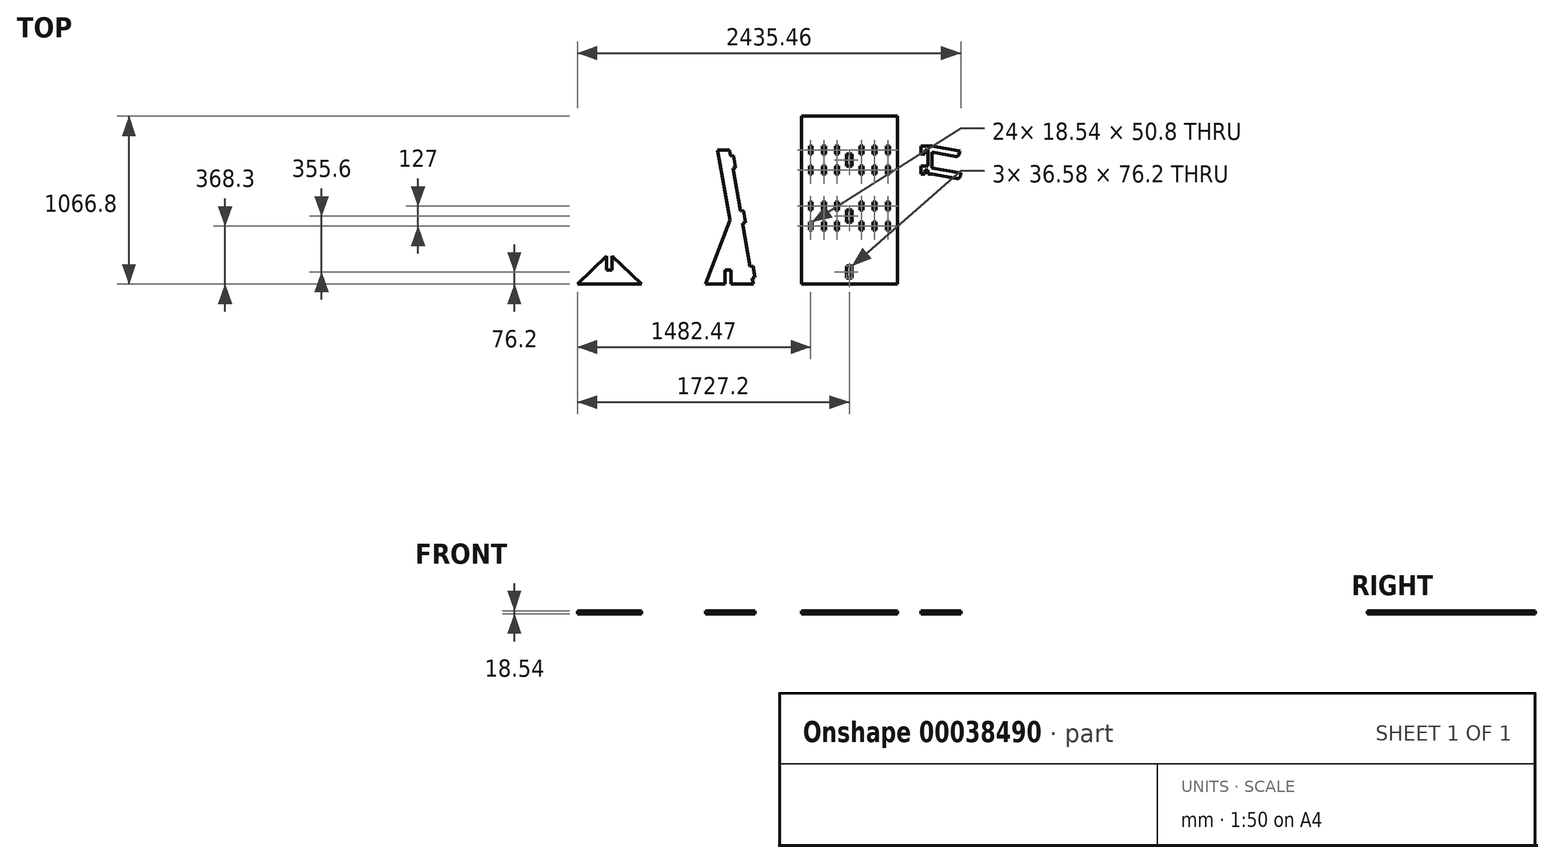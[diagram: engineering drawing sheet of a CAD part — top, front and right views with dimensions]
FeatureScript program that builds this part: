
annotation { "Feature Type Name" : "Feature", "Feature Type Description" : "" }
export const myFeature = defineFeature(function(context is Context, id is Id, definition is map)
    precondition{}
    {
        {
            var Q0;
            Q0=qCreatedBy(makeId("Top.planeOp"),FACE);
            var sketch = newSketch(context, id + "F0", { "sketchPlane" : qUnion([Q0])});
            skLineSegment(sketch, "E0", {"start": v(0, 0) * mm, "end": v(304.8, 0) * mm});
            skLineSegment(sketch, "E1", {"start": v(304.8, 0) * mm, "end": v(154.84, 850.48) * mm});
            skLineSegment(sketch, "E2", {"start": v(154.84, 850.48) * mm, "end": v(78.64, 850.48) * mm});
            skLineSegment(sketch, "E3", {"start": v(78.64, 850.48) * mm, "end": v(0, 0) * mm});
            skLineSegment(sketch, "E4", {"start": v(78.64, 850.48) * mm, "end": v(156.94, 406.4) * mm});
            skLineSegment(sketch, "E5", {"start": v(156.94, 406.4) * mm, "end": v(0, 0) * mm});
            skLineSegment(sketch, "E6", {"start": v(161.45, 812.96) * mm, "end": v(179.71, 816.18) * mm});
            skLineSegment(sketch, "E7", {"start": v(179.71, 816.18) * mm, "end": v(192.95, 741.14) * mm});
            skLineSegment(sketch, "E8", {"start": v(192.95, 741.14) * mm, "end": v(174.69, 737.92) * mm});
            skLineSegment(sketch, "E9", {"start": v(229.82, 425.24) * mm, "end": v(248.08, 428.46) * mm, "construction": true});
            skLineSegment(sketch, "E10.0", {"start": v(223.2, 462.76) * mm, "end": v(241.46, 465.98) * mm});
            skLineSegment(sketch, "E11.0", {"start": v(236.43, 387.72) * mm, "end": v(254.7, 390.94) * mm});
            skLineSegment(sketch, "E12", {"start": v(241.46, 465.98) * mm, "end": v(254.7, 390.94) * mm});
            skLineSegment(sketch, "E13.MirrorCS", {"start": v(298.18, 37.52) * mm, "end": v(316.44, 40.74) * mm});
            skLineSegment(sketch, "E14.MirrorCS", {"start": v(316.44, 40.74) * mm, "end": v(303.21, 115.78) * mm});
            skLineSegment(sketch, "E15.MirrorCS", {"start": v(303.21, 115.78) * mm, "end": v(284.95, 112.56) * mm});
            skLineSegment(sketch, "E16.bottom", {"start": v(127, 0) * mm, "end": v(164.08, 0) * mm});
            skLineSegment(sketch, "E16.top", {"start": v(127, 88.9) * mm, "end": v(164.08, 88.9) * mm});
            skLineSegment(sketch, "E16.left", {"start": v(127, 0) * mm, "end": v(127, 88.9) * mm});
            skLineSegment(sketch, "E16.right", {"start": v(164.08, 0) * mm, "end": v(164.08, 88.9) * mm});
            skLineSegment(sketch, "E17.bottom", {"start": v(609.6, 1066.8) * mm, "end": v(1219.2, 1066.8) * mm});
            skLineSegment(sketch, "E17.top", {"start": v(609.6, 0) * mm, "end": v(1219.2, 0) * mm});
            skLineSegment(sketch, "E17.left", {"start": v(609.6, 1066.8) * mm, "end": v(609.6, 0) * mm});
            skLineSegment(sketch, "E17.right", {"start": v(1219.2, 1066.8) * mm, "end": v(1219.2, 0) * mm});
            skLineSegment(sketch, "E18.bottom", {"start": v(896.11, 825.5) * mm, "end": v(932.69, 825.5) * mm});
            skLineSegment(sketch, "E18.top", {"start": v(896.11, 749.3) * mm, "end": v(932.69, 749.3) * mm});
            skLineSegment(sketch, "E18.left", {"start": v(896.11, 825.5) * mm, "end": v(896.11, 749.3) * mm});
            skLineSegment(sketch, "E18.right", {"start": v(932.69, 825.5) * mm, "end": v(932.69, 749.3) * mm});
            skLineSegment(sketch, "E19.bottom", {"start": v(896.11, 469.9) * mm, "end": v(932.69, 469.9) * mm});
            skLineSegment(sketch, "E19.top", {"start": v(896.11, 393.7) * mm, "end": v(932.69, 393.7) * mm});
            skLineSegment(sketch, "E19.left", {"start": v(896.11, 469.9) * mm, "end": v(896.11, 393.7) * mm});
            skLineSegment(sketch, "E19.right", {"start": v(932.69, 469.9) * mm, "end": v(932.69, 393.7) * mm});
            skLineSegment(sketch, "E20.bottom", {"start": v(896.11, 114.3) * mm, "end": v(932.69, 114.3) * mm});
            skLineSegment(sketch, "E20.top", {"start": v(896.11, 38.1) * mm, "end": v(932.69, 38.1) * mm});
            skLineSegment(sketch, "E20.left", {"start": v(896.11, 114.3) * mm, "end": v(896.11, 38.1) * mm});
            skLineSegment(sketch, "E20.right", {"start": v(932.69, 114.3) * mm, "end": v(932.69, 38.1) * mm});
            skLineSegment(sketch, "E21", {"start": v(914.4, 1066.8) * mm, "end": v(914.4, 825.5) * mm, "construction": true});
            skPoint(sketch, "E22", {"position": v(914.4, 825.5) * mm});
            skLineSegment(sketch, "E23.top", {"start": v(845.31, 469.9) * mm, "end": v(660.4, 469.9) * mm, "construction": true});
            skLineSegment(sketch, "E24", {"start": v(609.6, 431.8) * mm, "end": v(1219.2, 431.8) * mm, "construction": true});
            skPoint(sketch, "E24.startSnap0", {"position": v(896.11, 431.8) * mm});
            skLineSegment(sketch, "E25.bottom", {"start": v(660.4, 825.5) * mm, "end": v(845.31, 825.5) * mm, "construction": true});
            skLineSegment(sketch, "E25.top", {"start": v(660.4, 876.3) * mm, "end": v(845.31, 876.3) * mm, "construction": true});
            skLineSegment(sketch, "E25.left", {"start": v(660.4, 825.5) * mm, "end": v(660.4, 876.3) * mm});
            skLineSegment(sketch, "E25.right", {"start": v(845.31, 825.5) * mm, "end": v(845.31, 876.3) * mm});
            skLineSegment(sketch, "E26.bottom", {"start": v(660.4, 876.3) * mm, "end": v(678.94, 876.3) * mm});
            skLineSegment(sketch, "E26.top", {"start": v(660.4, 825.5) * mm, "end": v(678.94, 825.5) * mm});
            skLineSegment(sketch, "E26.left", {"start": v(660.4, 876.3) * mm, "end": v(660.4, 825.5) * mm});
            skLineSegment(sketch, "E26.right", {"start": v(678.94, 876.3) * mm, "end": v(678.94, 825.5) * mm});
            skLineSegment(sketch, "E27.bottom", {"start": v(762.13, 876.3) * mm, "end": v(743.58, 876.3) * mm});
            skLineSegment(sketch, "E27.top", {"start": v(762.13, 825.5) * mm, "end": v(743.58, 825.5) * mm});
            skLineSegment(sketch, "E27.left", {"start": v(762.13, 876.3) * mm, "end": v(762.13, 825.5) * mm});
            skLineSegment(sketch, "E27.right", {"start": v(743.58, 876.3) * mm, "end": v(743.58, 825.5) * mm});
            skPoint(sketch, "E27.middle", {"position": v(752.86, 850.9) * mm});
            skPoint(sketch, "E27.middle.positionSnap0", {"position": v(660.4, 850.9) * mm});
            skPoint(sketch, "E27.middle.positionSnap1", {"position": v(752.86, 825.5) * mm});
            skPoint(sketch, "E27.centerSnap0", {"position": v(660.4, 850.9) * mm});
            skPoint(sketch, "E27.centerSnap1", {"position": v(752.86, 825.5) * mm});
            skLineSegment(sketch, "E28.bottom", {"start": v(845.31, 876.3) * mm, "end": v(826.77, 876.3) * mm});
            skLineSegment(sketch, "E28.top", {"start": v(845.31, 825.5) * mm, "end": v(826.77, 825.5) * mm});
            skLineSegment(sketch, "E28.left", {"start": v(845.31, 876.3) * mm, "end": v(845.31, 825.5) * mm});
            skLineSegment(sketch, "E28.right", {"start": v(826.77, 876.3) * mm, "end": v(826.77, 825.5) * mm});
            skLineSegment(sketch, "E29.bottom", {"start": v(660.4, 749.3) * mm, "end": v(845.31, 749.3) * mm, "construction": true});
            skLineSegment(sketch, "E29.top", {"start": v(660.4, 698.5) * mm, "end": v(845.31, 698.5) * mm, "construction": true});
            skLineSegment(sketch, "E29.left", {"start": v(660.4, 749.3) * mm, "end": v(660.4, 698.5) * mm});
            skLineSegment(sketch, "E29.right", {"start": v(845.31, 749.3) * mm, "end": v(845.31, 698.5) * mm});
            skLineSegment(sketch, "E30.top", {"start": v(660.4, 520.7) * mm, "end": v(845.31, 520.7) * mm, "construction": true});
            skLineSegment(sketch, "E30.left", {"start": v(660.4, 469.9) * mm, "end": v(660.4, 520.7) * mm});
            skLineSegment(sketch, "E30.right", {"start": v(845.31, 469.9) * mm, "end": v(845.31, 520.7) * mm});
            skLineSegment(sketch, "E31.MirrorCS", {"start": v(660.4, 342.9) * mm, "end": v(845.31, 342.9) * mm, "construction": true});
            skLineSegment(sketch, "E32.MirrorCS", {"start": v(845.31, 393.7) * mm, "end": v(845.31, 342.9) * mm});
            skLineSegment(sketch, "E33.MirrorCS", {"start": v(845.31, 393.7) * mm, "end": v(660.4, 393.7) * mm, "construction": true});
            skLineSegment(sketch, "E34.MirrorCS", {"start": v(660.4, 393.7) * mm, "end": v(660.4, 342.9) * mm});
            skLineSegment(sketch, "E35.bottom", {"start": v(660.4, 749.3) * mm, "end": v(678.94, 749.3) * mm});
            skLineSegment(sketch, "E35.top", {"start": v(660.4, 698.5) * mm, "end": v(678.94, 698.5) * mm});
            skLineSegment(sketch, "E35.right", {"start": v(678.94, 749.3) * mm, "end": v(678.94, 698.5) * mm});
            skLineSegment(sketch, "E36.bottom", {"start": v(845.31, 749.3) * mm, "end": v(826.77, 749.3) * mm});
            skLineSegment(sketch, "E36.top", {"start": v(845.31, 698.5) * mm, "end": v(826.77, 698.5) * mm});
            skLineSegment(sketch, "E36.right", {"start": v(826.77, 749.3) * mm, "end": v(826.77, 698.5) * mm});
            skLineSegment(sketch, "E37.bottom", {"start": v(845.31, 520.7) * mm, "end": v(826.77, 520.7) * mm});
            skLineSegment(sketch, "E37.top", {"start": v(845.31, 469.9) * mm, "end": v(826.77, 469.9) * mm});
            skLineSegment(sketch, "E37.left", {"start": v(845.31, 520.7) * mm, "end": v(845.31, 469.9) * mm});
            skLineSegment(sketch, "E37.right", {"start": v(826.77, 520.7) * mm, "end": v(826.77, 469.9) * mm});
            skLineSegment(sketch, "E38.bottom", {"start": v(845.31, 393.7) * mm, "end": v(826.77, 393.7) * mm});
            skLineSegment(sketch, "E38.top", {"start": v(845.31, 342.9) * mm, "end": v(826.77, 342.9) * mm});
            skLineSegment(sketch, "E38.right", {"start": v(826.77, 393.7) * mm, "end": v(826.77, 342.9) * mm});
            skLineSegment(sketch, "E39.bottom", {"start": v(660.4, 393.7) * mm, "end": v(678.94, 393.7) * mm});
            skLineSegment(sketch, "E39.top", {"start": v(660.4, 342.9) * mm, "end": v(678.94, 342.9) * mm});
            skLineSegment(sketch, "E39.right", {"start": v(678.94, 393.7) * mm, "end": v(678.94, 342.9) * mm});
            skLineSegment(sketch, "E40.bottom", {"start": v(660.4, 469.9) * mm, "end": v(678.94, 469.9) * mm});
            skLineSegment(sketch, "E40.top", {"start": v(660.4, 520.7) * mm, "end": v(678.94, 520.7) * mm});
            skLineSegment(sketch, "E40.right", {"start": v(678.94, 469.9) * mm, "end": v(678.94, 520.7) * mm});
            skLineSegment(sketch, "E41.bottom", {"start": v(743.58, 749.3) * mm, "end": v(762.13, 749.3) * mm});
            skLineSegment(sketch, "E41.top", {"start": v(743.58, 698.5) * mm, "end": v(762.13, 698.5) * mm});
            skLineSegment(sketch, "E41.left", {"start": v(743.58, 749.3) * mm, "end": v(743.58, 698.5) * mm});
            skLineSegment(sketch, "E41.right", {"start": v(762.13, 749.3) * mm, "end": v(762.13, 698.5) * mm});
            skPoint(sketch, "E41.middle", {"position": v(752.86, 723.9) * mm});
            skPoint(sketch, "E41.middle.positionSnap0", {"position": v(678.94, 723.9) * mm});
            skPoint(sketch, "E41.middle.positionSnap1", {"position": v(752.86, 749.3) * mm});
            skPoint(sketch, "E41.centerSnap0", {"position": v(678.94, 723.9) * mm});
            skPoint(sketch, "E41.centerSnap1", {"position": v(752.86, 749.3) * mm});
            skLineSegment(sketch, "E42.bottom", {"start": v(743.58, 520.7) * mm, "end": v(762.13, 520.7) * mm});
            skLineSegment(sketch, "E42.top", {"start": v(743.58, 469.9) * mm, "end": v(762.13, 469.9) * mm});
            skLineSegment(sketch, "E42.left", {"start": v(743.58, 520.7) * mm, "end": v(743.58, 469.9) * mm});
            skLineSegment(sketch, "E42.right", {"start": v(762.13, 520.7) * mm, "end": v(762.13, 469.9) * mm});
            skPoint(sketch, "E42.middle", {"position": v(752.86, 495.3) * mm});
            skPoint(sketch, "E42.middle.positionSnap0", {"position": v(678.94, 495.3) * mm});
            skPoint(sketch, "E42.middle.positionSnap1", {"position": v(752.86, 520.7) * mm});
            skPoint(sketch, "E42.centerSnap0", {"position": v(678.94, 495.3) * mm});
            skPoint(sketch, "E42.centerSnap1", {"position": v(752.86, 520.7) * mm});
            skLineSegment(sketch, "E43.bottom", {"start": v(743.58, 393.7) * mm, "end": v(762.13, 393.7) * mm});
            skLineSegment(sketch, "E43.top", {"start": v(743.58, 342.9) * mm, "end": v(762.13, 342.9) * mm});
            skLineSegment(sketch, "E43.left", {"start": v(743.58, 393.7) * mm, "end": v(743.58, 342.9) * mm});
            skLineSegment(sketch, "E43.right", {"start": v(762.13, 393.7) * mm, "end": v(762.13, 342.9) * mm});
            skPoint(sketch, "E43.middle", {"position": v(752.86, 368.3) * mm});
            skPoint(sketch, "E43.middle.positionSnap0", {"position": v(678.94, 368.3) * mm});
            skPoint(sketch, "E43.middle.positionSnap1", {"position": v(752.86, 393.7) * mm});
            skPoint(sketch, "E43.centerSnap0", {"position": v(678.94, 368.3) * mm});
            skPoint(sketch, "E43.centerSnap1", {"position": v(752.86, 393.7) * mm});
            skLineSegment(sketch, "E44.MirrorCS", {"start": v(1168.4, 876.3) * mm, "end": v(1149.86, 876.3) * mm});
            skLineSegment(sketch, "E45.MirrorCS", {"start": v(1168.4, 825.5) * mm, "end": v(1168.4, 876.3) * mm});
            skLineSegment(sketch, "E46.MirrorCS", {"start": v(1149.86, 876.3) * mm, "end": v(1149.86, 825.5) * mm});
            skLineSegment(sketch, "E47.MirrorCS", {"start": v(1168.4, 825.5) * mm, "end": v(1149.86, 825.5) * mm});
            skLineSegment(sketch, "E48.MirrorCS", {"start": v(1066.67, 825.5) * mm, "end": v(1085.21, 825.5) * mm});
            skPoint(sketch, "E49.MirrorP", {"position": v(1075.94, 825.5) * mm});
            skLineSegment(sketch, "E50.MirrorCS", {"start": v(1085.22, 876.3) * mm, "end": v(1085.22, 825.5) * mm});
            skLineSegment(sketch, "E51.MirrorCS", {"start": v(1066.67, 876.3) * mm, "end": v(1066.67, 825.5) * mm});
            skPoint(sketch, "E52.MirrorP", {"position": v(1075.94, 850.9) * mm});
            skLineSegment(sketch, "E53.MirrorCS", {"start": v(1066.67, 876.3) * mm, "end": v(1085.21, 876.3) * mm});
            skLineSegment(sketch, "E54.MirrorCS", {"start": v(983.49, 876.3) * mm, "end": v(1002.03, 876.3) * mm});
            skLineSegment(sketch, "E55.MirrorCS", {"start": v(983.49, 876.3) * mm, "end": v(983.49, 825.5) * mm});
            skLineSegment(sketch, "E56.MirrorCS", {"start": v(983.49, 825.5) * mm, "end": v(1002.03, 825.5) * mm});
            skLineSegment(sketch, "E57.MirrorCS", {"start": v(1002.03, 876.3) * mm, "end": v(1002.03, 825.5) * mm});
            skLineSegment(sketch, "E58.MirrorCS", {"start": v(983.49, 749.3) * mm, "end": v(983.49, 698.5) * mm});
            skLineSegment(sketch, "E59.MirrorCS", {"start": v(1168.4, 749.3) * mm, "end": v(1168.4, 698.5) * mm});
            skLineSegment(sketch, "E60.MirrorCS", {"start": v(1168.4, 469.9) * mm, "end": v(1168.4, 520.7) * mm});
            skLineSegment(sketch, "E61.MirrorCS", {"start": v(983.49, 520.7) * mm, "end": v(983.49, 469.9) * mm});
            skLineSegment(sketch, "E62.MirrorCS", {"start": v(1168.4, 749.3) * mm, "end": v(1149.86, 749.3) * mm});
            skLineSegment(sketch, "E63.MirrorCS", {"start": v(1168.4, 698.5) * mm, "end": v(1149.86, 698.5) * mm});
            skLineSegment(sketch, "E64.MirrorCS", {"start": v(1085.21, 749.3) * mm, "end": v(1066.67, 749.3) * mm});
            skPoint(sketch, "E65.MirrorP", {"position": v(1075.94, 749.3) * mm});
            skLineSegment(sketch, "E66.MirrorCS", {"start": v(1066.67, 749.3) * mm, "end": v(1066.67, 698.5) * mm});
            skLineSegment(sketch, "E67.MirrorCS", {"start": v(1085.21, 698.5) * mm, "end": v(1066.67, 698.5) * mm});
            skPoint(sketch, "E68.MirrorP", {"position": v(1075.94, 723.9) * mm});
            skLineSegment(sketch, "E69.MirrorCS", {"start": v(1085.22, 749.3) * mm, "end": v(1085.22, 698.5) * mm});
            skPoint(sketch, "E70.MirrorP", {"position": v(1075.94, 495.3) * mm});
            skPoint(sketch, "E71.MirrorP", {"position": v(1075.94, 520.7) * mm});
            skLineSegment(sketch, "E72.MirrorCS", {"start": v(1066.67, 520.7) * mm, "end": v(1066.67, 469.9) * mm});
            skLineSegment(sketch, "E73.MirrorCS", {"start": v(1085.22, 520.7) * mm, "end": v(1066.67, 520.7) * mm});
            skLineSegment(sketch, "E74.MirrorCS", {"start": v(1085.22, 469.9) * mm, "end": v(1066.67, 469.9) * mm});
            skLineSegment(sketch, "E75.MirrorCS", {"start": v(1085.22, 520.7) * mm, "end": v(1085.22, 469.9) * mm});
            skLineSegment(sketch, "E76.MirrorCS", {"start": v(983.49, 749.3) * mm, "end": v(1002.03, 749.3) * mm});
            skLineSegment(sketch, "E77.MirrorCS", {"start": v(1002.03, 749.3) * mm, "end": v(1002.03, 698.5) * mm});
            skLineSegment(sketch, "E78.MirrorCS", {"start": v(983.49, 698.5) * mm, "end": v(1002.03, 698.5) * mm});
            skLineSegment(sketch, "E79.MirrorCS", {"start": v(1149.86, 749.3) * mm, "end": v(1149.86, 698.5) * mm});
            skLineSegment(sketch, "E80.MirrorCS", {"start": v(983.49, 520.7) * mm, "end": v(1002.03, 520.7) * mm});
            skLineSegment(sketch, "E81.MirrorCS", {"start": v(1002.03, 520.7) * mm, "end": v(1002.03, 469.9) * mm});
            skLineSegment(sketch, "E82.MirrorCS", {"start": v(983.49, 469.9) * mm, "end": v(1002.03, 469.9) * mm});
            skLineSegment(sketch, "E83.MirrorCS", {"start": v(1168.4, 520.7) * mm, "end": v(1149.86, 520.7) * mm});
            skLineSegment(sketch, "E84.MirrorCS", {"start": v(1149.86, 469.9) * mm, "end": v(1149.86, 520.7) * mm});
            skLineSegment(sketch, "E85.MirrorCS", {"start": v(1168.4, 469.9) * mm, "end": v(1149.86, 469.9) * mm});
            skLineSegment(sketch, "E86.MirrorCS", {"start": v(1168.4, 393.7) * mm, "end": v(1168.4, 342.9) * mm});
            skLineSegment(sketch, "E87.MirrorCS", {"start": v(1168.4, 393.7) * mm, "end": v(1149.86, 393.7) * mm});
            skLineSegment(sketch, "E88.MirrorCS", {"start": v(1149.86, 393.7) * mm, "end": v(1149.86, 342.9) * mm});
            skLineSegment(sketch, "E89.MirrorCS", {"start": v(1168.4, 342.9) * mm, "end": v(1149.86, 342.9) * mm});
            skLineSegment(sketch, "E90.MirrorCS", {"start": v(1085.22, 393.7) * mm, "end": v(1066.67, 393.7) * mm});
            skPoint(sketch, "E91.MirrorP", {"position": v(1075.94, 393.7) * mm});
            skLineSegment(sketch, "E92.MirrorCS", {"start": v(1085.22, 342.9) * mm, "end": v(1066.67, 342.9) * mm});
            skPoint(sketch, "E93.MirrorP", {"position": v(1075.94, 368.3) * mm});
            skLineSegment(sketch, "E94.MirrorCS", {"start": v(1066.67, 393.7) * mm, "end": v(1066.67, 342.9) * mm});
            skLineSegment(sketch, "E95.MirrorCS", {"start": v(1085.22, 393.7) * mm, "end": v(1085.22, 342.9) * mm});
            skLineSegment(sketch, "E96.MirrorCS", {"start": v(1002.03, 393.7) * mm, "end": v(1002.03, 342.9) * mm});
            skLineSegment(sketch, "E97.MirrorCS", {"start": v(983.49, 393.7) * mm, "end": v(1002.03, 393.7) * mm});
            skLineSegment(sketch, "E98.MirrorCS", {"start": v(983.49, 393.7) * mm, "end": v(983.49, 342.9) * mm});
            skLineSegment(sketch, "E99.MirrorCS", {"start": v(983.49, 342.9) * mm, "end": v(1002.03, 342.9) * mm});
            skLineSegment(sketch, "E100.bottom", {"start": v(1371.6, 825.5) * mm, "end": v(1397, 825.5) * mm});
            skLineSegment(sketch, "E100.top", {"start": v(1371.6, 876.3) * mm, "end": v(1397, 876.3) * mm});
            skLineSegment(sketch, "E100.left", {"start": v(1371.6, 825.5) * mm, "end": v(1371.6, 876.3) * mm});
            skLineSegment(sketch, "E100.right", {"start": v(1397, 825.5) * mm, "end": v(1397, 876.3) * mm});
            skLineSegment(sketch, "E101.bottom", {"start": v(1397, 850.9) * mm, "end": v(1415.54, 850.9) * mm});
            skLineSegment(sketch, "E101.top", {"start": v(1397, 876.3) * mm, "end": v(1415.54, 876.3) * mm});
            skLineSegment(sketch, "E101.left", {"start": v(1397, 850.9) * mm, "end": v(1397, 876.3) * mm});
            skLineSegment(sketch, "E101.right", {"start": v(1415.54, 850.9) * mm, "end": v(1415.54, 876.3) * mm});
            skLineSegment(sketch, "E102.bottom", {"start": v(1371.6, 749.3) * mm, "end": v(1397, 749.3) * mm});
            skLineSegment(sketch, "E102.top", {"start": v(1371.6, 698.5) * mm, "end": v(1397, 698.5) * mm});
            skLineSegment(sketch, "E102.left", {"start": v(1371.6, 749.3) * mm, "end": v(1371.6, 698.5) * mm});
            skLineSegment(sketch, "E102.right", {"start": v(1397, 749.3) * mm, "end": v(1397, 698.5) * mm});
            skPoint(sketch, "E103.oppositeSnap0", {"position": v(1397, 723.9) * mm});
            skLineSegment(sketch, "E103.bottom", {"start": v(1397, 749.3) * mm, "end": v(1415.54, 749.3) * mm});
            skLineSegment(sketch, "E103.top", {"start": v(1397, 723.9) * mm, "end": v(1415.54, 723.9) * mm});
            skLineSegment(sketch, "E103.left", {"start": v(1397, 749.3) * mm, "end": v(1397, 723.9) * mm});
            skLineSegment(sketch, "E103.right", {"start": v(1415.54, 749.3) * mm, "end": v(1415.54, 723.9) * mm});
            skLineSegment(sketch, "E104.bottom", {"start": v(1415.54, 698.5) * mm, "end": v(1440.94, 698.5) * mm});
            skLineSegment(sketch, "E104.top", {"start": v(1415.54, 876.3) * mm, "end": v(1440.94, 876.3) * mm});
            skLineSegment(sketch, "E104.left", {"start": v(1415.54, 698.5) * mm, "end": v(1415.54, 876.3) * mm});
            skLineSegment(sketch, "E104.right", {"start": v(1440.94, 698.5) * mm, "end": v(1440.94, 876.3) * mm});
            skLineSegment(sketch, "E105", {"start": v(1440.94, 876.3) * mm, "end": v(1616.04, 845.43) * mm});
            skLineSegment(sketch, "E106.0", {"start": v(1440.94, 837.61) * mm, "end": v(1590.66, 811.21) * mm});
            skLineSegment(sketch, "E107", {"start": v(1612.73, 826.66) * mm, "end": v(1616.04, 845.43) * mm});
            skLineSegment(sketch, "E108", {"start": v(1440.94, 698.5) * mm, "end": v(1597.28, 670.93) * mm});
            skLineSegment(sketch, "E109.0", {"start": v(1440.94, 737.19) * mm, "end": v(1622.66, 705.15) * mm});
            skLineSegment(sketch, "E110", {"start": v(1619.35, 686.39) * mm, "end": v(1622.66, 705.15) * mm});
            skPoint(sketch, "E111.visualSharp", {"position": v(1609.42, 807.9) * mm});
            skArc(sketch, "E111.filletArc", {"start": v(1590.66, 811.21) * mm, "mid": v(1604.9, 814.37) * mm, "end": v(1612.73, 826.66) * mm});
            skPoint(sketch, "E112.visualSharp", {"position": v(1616.04, 667.63) * mm});
            skArc(sketch, "E112.filletArc", {"start": v(1597.28, 670.93) * mm, "mid": v(1611.51, 674.09) * mm, "end": v(1619.35, 686.39) * mm});
            skPoint(sketch, "E113.cCircle.centerSnap0", {"position": v(145.54, 0) * mm});
            skPoint(sketch, "E113.0.midPoint", {"position": v(-609.6, 88.9) * mm});
            skLineSegment(sketch, "E114", {"start": v(-406.4, 0) * mm, "end": v(-812.8, 0) * mm});
            skLineSegment(sketch, "E115", {"start": v(-812.8, 0) * mm, "end": v(-609.6, 195.38) * mm});
            skLineSegment(sketch, "E116", {"start": v(-609.6, 195.38) * mm, "end": v(-406.4, 0) * mm});
            skLineSegment(sketch, "E117.bottom", {"start": v(-591.31, 88.9) * mm, "end": v(-627.89, 88.9) * mm});
            skLineSegment(sketch, "E117.left", {"start": v(-591.31, 88.9) * mm, "end": v(-591.31, 177.8) * mm});
            skLineSegment(sketch, "E117.right", {"start": v(-627.89, 88.9) * mm, "end": v(-627.89, 177.8) * mm});
            skSolve(sketch);
        }
        {
            var Q0;
            {var subQ10=sQuery(id+"F0.wireOp",EDGE,"E2");Q0=makeQuery(id+"F0.imprint","IMPRINT",FACE,{"disambiguationData":[TD([[makeQuery(id+"F0.imprint","IMPRINT",EDGE,{"derivedFrom":subQ10}),1.0]])]});}
            var Q1;
            {var subQ0=sQuery(id+"F0.wireOp",EDGE,"E6");Q1=makeQuery(id+"F0.imprint","IMPRINT",FACE,{"disambiguationData":[TD([[makeQuery(id+"F0.imprint","IMPRINT",EDGE,{"derivedFrom":subQ0}),-1.0]])]});}
            var Q2;
            {var subQ0=sQuery(id+"F0.wireOp",EDGE,"E10.0");Q2=makeQuery(id+"F0.imprint","IMPRINT",FACE,{"disambiguationData":[TD([[makeQuery(id+"F0.imprint","IMPRINT",EDGE,{"derivedFrom":subQ0}),-1.0]])]});}
            var Q3;
            {var subQ0=sQuery(id+"F0.wireOp",EDGE,"E13.MirrorCS");Q3=makeQuery(id+"F0.imprint","IMPRINT",FACE,{"disambiguationData":[TD([[makeQuery(id+"F0.imprint","IMPRINT",EDGE,{"derivedFrom":subQ0}),1.0]])]});}
            var Q4;
            Q4=makeQuery(id+"F0.imprint","IMPRINT",FACE,{"disambiguationData":[TD([[makeQuery(id+"F0.imprint","IMPRINT",EDGE,{"derivedFrom":sQuery(id+"F0.wireOp",EDGE,"E17.bottom")}),-1.0]])]});
            var Q5;
            {var subQ1=sQuery(id+"F0.wireOp",EDGE,"E105");Q5=makeQuery(id+"F0.imprint","IMPRINT",FACE,{"disambiguationData":[TD([[makeQuery(id+"F0.imprint","IMPRINT",EDGE,{"derivedFrom":subQ1}),-1.0]])]});}
            var Q6;
            {var subQ3=sQuery(id+"F0.wireOp",EDGE,"E104.bottom");Q6=makeQuery(id+"F0.imprint","IMPRINT",FACE,{"disambiguationData":[TD([[makeQuery(id+"F0.imprint","IMPRINT",EDGE,{"derivedFrom":subQ3}),1.0]])]});}
            var Q7;
            {var subQ0=sQuery(id+"F0.wireOp",EDGE,"E101.bottom");Q7=makeQuery(id+"F0.imprint","IMPRINT",FACE,{"disambiguationData":[TD([[makeQuery(id+"F0.imprint","IMPRINT",EDGE,{"derivedFrom":subQ0}),1.0]])]});}
            var Q8;
            Q8=makeQuery(id+"F0.imprint","IMPRINT",FACE,{"disambiguationData":[TD([[makeQuery(id+"F0.imprint","IMPRINT",EDGE,{"derivedFrom":sQuery(id+"F0.wireOp",EDGE,"E100.bottom")}),1.0]])]});
            var Q9;
            Q9=makeQuery(id+"F0.imprint","IMPRINT",FACE,{"disambiguationData":[TD([[makeQuery(id+"F0.imprint","IMPRINT",EDGE,{"derivedFrom":sQuery(id+"F0.wireOp",EDGE,"E102.bottom")}),-1.0]])]});
            var Q10;
            {var subQ0=sQuery(id+"F0.wireOp",EDGE,"E103.bottom");Q10=makeQuery(id+"F0.imprint","IMPRINT",FACE,{"disambiguationData":[TD([[makeQuery(id+"F0.imprint","IMPRINT",EDGE,{"derivedFrom":subQ0}),-1.0]])]});}
            var Q11;
            {var subQ1=sQuery(id+"F0.wireOp",EDGE,"E108");Q11=makeQuery(id+"F0.imprint","IMPRINT",FACE,{"disambiguationData":[TD([[makeQuery(id+"F0.imprint","IMPRINT",EDGE,{"derivedFrom":subQ1}),1.0]])]});}
            var Q12;
            {var subQ1=sQuery(id+"F0.wireOp",EDGE,"E114");Q12=makeQuery(id+"F0.imprint","IMPRINT",FACE,{"disambiguationData":[TD([[makeQuery(id+"F0.imprint","IMPRINT",EDGE,{"derivedFrom":subQ1}),-1.0]])]});}
            extrude(context, id + "F1", {"entities" : qUnion([Q0, Q1, Q2, Q3, Q4, Q5, Q6, Q7, Q8, Q9, Q10, Q11, Q12]), "depth" : 18.54 * mm});
        }
    });
